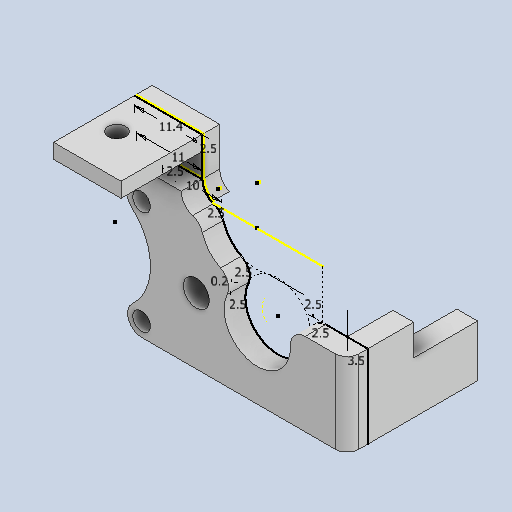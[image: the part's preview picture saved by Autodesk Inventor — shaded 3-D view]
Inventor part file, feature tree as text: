
AUTODESK INVENTOR PART (.ipt)
format: ipt  version: 2022 (Build 260153070, 153G)  size: 214,528 bytes
history: native  units: mm
features: reference x12, extrude x7, sketch x5, other x4, fillet x1, projected_geometry x1
ambient origin geometry x8: Origin, YZ Plane, XZ Plane, XY Plane, X Axis, Y Axis, Z Axis, Center Point
bodies: Solid1 (feature_tree)
feature tree (30):
  sketch  "Sketch1"  dims[d0=0.2mm d1=2.5mm]
  extrude  "Extrusion1"  Depth=2.5mm
  extrude  "Extrusion2"  Depth=10.0mm
  fillet  "Fillet1"  Radius=2.5mm
  extrude  "Extrusion3"  Depth=2.5mm
  sketch  "Sketch5"  dims[d6=2.5mm d7=2.5mm]
  extrude  "Extrusion4"  Depth=3.5mm TaperAngle=0.0deg
  extrude  "Extrusion5"  Depth=2.0mm
  extrude  "Extrusion6"  Depth=2.5mm
  extrude  "Extrusion7"  Depth=2.5mm
  reference  "Reference1"
  reference  "Reference2"
  reference  "Reference3"
  reference  "Reference4"
  reference  "Reference5"
  reference  "Reference6"
  reference  "Reference7"
  sketch  "Sketch2"  dims[d3=3.5mm d4=10.0mm d5=2.5mm]
  reference  "Reference8"
  reference  "Reference10"
  reference  "Reference11"
  projected_geometry  "Projected Loop1"
  sketch  "Sketch6"  dims[d8=2.5mm d9=3.5mm d10=0.0mm]
  reference  "Reference12"
  sketch  "Sketch7"  dims[d11=18.55mm d12=0.0mm d13=2.0mm d16=2.5mm d17=2.5mm d18=11.0mm d19=11.4mm d20=0.325mm d21=0.0mm d22=2.675mm d23=0.0mm d24=14.0mm d25=0.0mm d26=14.0mm d27=0.0mm d28=10.0mm d29=0.0mm]
  reference  "Reference13"
  other  "<userpath> laptop\Desktop\SumoBot\sumobotENCODER\MotorEncoderAssembly.iam"
  other  "MotorEncoderAssembly.iam"
  other  "TT motor output:1"
  other  "LM393 encoder:1"
